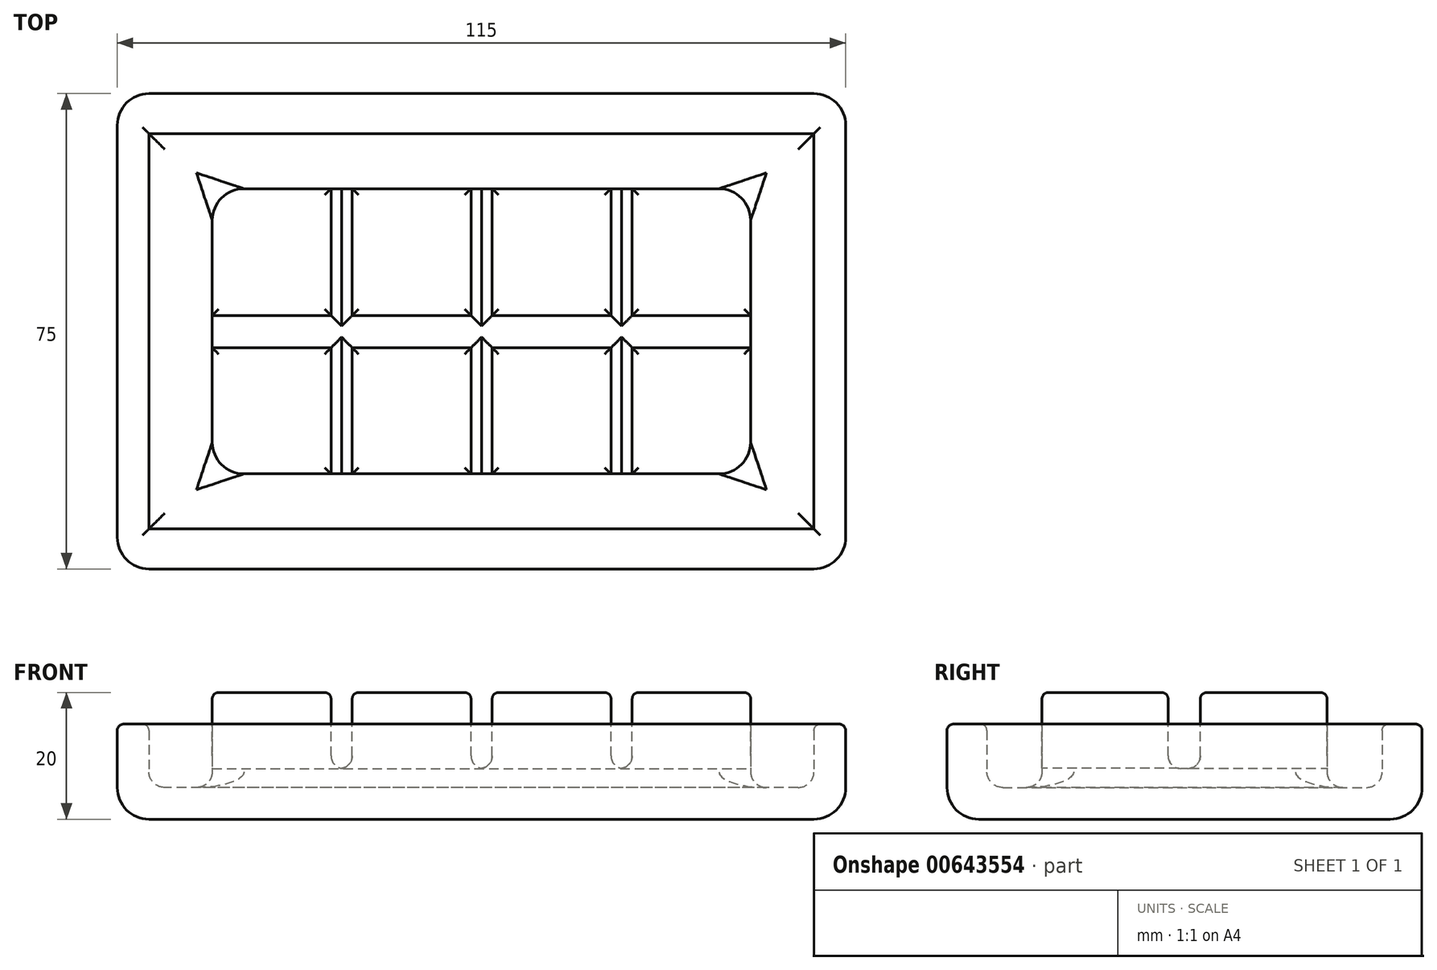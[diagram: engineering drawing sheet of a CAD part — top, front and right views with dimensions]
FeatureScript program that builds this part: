
annotation { "Feature Type Name" : "Feature", "Feature Type Description" : "" }
export const myFeature = defineFeature(function(context is Context, id is Id, definition is map)
    precondition{}
    {
        {
            var Q0;
            Q0=qCreatedBy(makeId("Top.planeOp"),FACE);
            var sketch = newSketch(context, id + "F0", { "sketchPlane" : qUnion([Q0])});
            skLineSegment(sketch, "E0.bottom", {"start": v(57.5, -37.5) * mm, "end": v(-57.5, -37.5) * mm});
            skLineSegment(sketch, "E0.top", {"start": v(57.5, 37.5) * mm, "end": v(-57.5, 37.5) * mm});
            skLineSegment(sketch, "E0.left", {"start": v(57.5, -37.5) * mm, "end": v(57.5, 37.5) * mm});
            skLineSegment(sketch, "E0.right", {"start": v(-57.5, -37.5) * mm, "end": v(-57.5, 37.5) * mm});
            skPoint(sketch, "E0.middle", {"position": v(0, 0) * mm});
            skSolve(sketch);
        }
        {
            var Q0;
            Q0=makeQuery(id+"F0.imprint","IMPRINT",FACE,{"disambiguationData":[TD([[makeQuery(id+"F0.imprint","IMPRINT",EDGE,{"derivedFrom":sQuery(id+"F0.wireOp",EDGE,"E0.bottom")}),-1.0]])]});
            extrude(context, id + "F1", {"entities" : qUnion([Q0]), "depth" : 5 * mm, "offsetDistance" : 25 * mm});
        }
        {
            var Q0;
            Q0=makeQuery(id+"F1.opExtrude","CAP_FACE",FACE,{"disambiguationData":[OSD([sQuery(id+"F0.wireOp",EDGE,"E0.bottom"),sQuery(id+"F0.wireOp",EDGE,"E0.top"),sQuery(id+"F0.wireOp",EDGE,"E0.left"),sQuery(id+"F0.wireOp",EDGE,"E0.right")])],"isStart":false});
            var sketch = newSketch(context, id + "F2", { "sketchPlane" : qUnion([Q0])});
            skLineSegment(sketch, "E1.bottom", {"start": v(52.5, -31.2) * mm, "end": v(-52.5, -31.2) * mm});
            skLineSegment(sketch, "E1.top", {"start": v(52.5, 31.2) * mm, "end": v(-52.5, 31.2) * mm});
            skLineSegment(sketch, "E1.left", {"start": v(52.5, -31.2) * mm, "end": v(52.5, 31.2) * mm});
            skLineSegment(sketch, "E1.right", {"start": v(-52.5, -31.2) * mm, "end": v(-52.5, 31.2) * mm});
            skPoint(sketch, "E1.middle", {"position": v(0, 0) * mm});
            skSolve(sketch);
        }
        {
            var Q0;
            Q0=makeQuery(id+"F2.imprint","IMPRINT",FACE,{"disambiguationData":[TD([[makeQuery(id+"F2.imprint","IMPRINT",EDGE,{"derivedFrom":sQuery(id+"F2.wireOp",EDGE,"E1.bottom")}),1.0]])]});
            extrude(context, id + "F3", {"entities" : qUnion([Q0]), "operationType" : NewBodyOperationType.ADD, "depth" : 10 * mm, "offsetDistance" : 25 * mm});
        }
        {
            var Q0;
            Q0=makeQuery(id+"F1.opExtrude","CAP_FACE",FACE,{"disambiguationData":[OSD([sQuery(id+"F0.wireOp",EDGE,"E0.bottom"),sQuery(id+"F0.wireOp",EDGE,"E0.top"),sQuery(id+"F0.wireOp",EDGE,"E0.left"),sQuery(id+"F0.wireOp",EDGE,"E0.right")])],"isStart":false});
            var sketch = newSketch(context, id + "F4", { "sketchPlane" : qUnion([Q0])});
            skLineSegment(sketch, "E2.bottom", {"start": v(42.5, 22.5) * mm, "end": v(-42.5, 22.5) * mm});
            skLineSegment(sketch, "E2.top", {"start": v(42.5, -22.5) * mm, "end": v(-42.5, -22.5) * mm});
            skLineSegment(sketch, "E2.left", {"start": v(42.5, 22.5) * mm, "end": v(42.5, -22.5) * mm});
            skLineSegment(sketch, "E2.right", {"start": v(-42.5, 22.5) * mm, "end": v(-42.5, -22.5) * mm});
            skPoint(sketch, "E2.middle", {"position": v(0, 0) * mm});
            skSolve(sketch);
        }
        {
            var Q0;
            Q0=makeQuery(id+"F4.imprint","IMPRINT",FACE,{"disambiguationData":[TD([[makeQuery(id+"F4.imprint","IMPRINT",EDGE,{"derivedFrom":sQuery(id+"F4.wireOp",EDGE,"E2.bottom")}),1.0]])]});
            extrude(context, id + "F5", {"entities" : qUnion([Q0]), "operationType" : NewBodyOperationType.ADD, "depth" : 15 * mm, "offsetDistance" : 25 * mm});
        }
        {
            var Q0;
            Q0=makeQuery(id+"F5.opExtrude","CAP_FACE",FACE,{"disambiguationData":[OSD([sQuery(id+"F4.wireOp",EDGE,"E2.bottom"),sQuery(id+"F4.wireOp",EDGE,"E2.top"),sQuery(id+"F4.wireOp",EDGE,"E2.left"),sQuery(id+"F4.wireOp",EDGE,"E2.right")])],"isStart":false});
            var sketch = newSketch(context, id + "F6", { "sketchPlane" : qUnion([Q0])});
            skLineSegment(sketch, "E3.bottom", {"start": v(-42.5, 22.5) * mm, "end": v(-23.75, 22.5) * mm});
            skLineSegment(sketch, "E3.top", {"start": v(-42.5, 2.5) * mm, "end": v(-23.75, 2.5) * mm});
            skLineSegment(sketch, "E3.left", {"start": v(-42.5, 22.5) * mm, "end": v(-42.5, 2.5) * mm});
            skLineSegment(sketch, "E3.right", {"start": v(-23.75, 22.5) * mm, "end": v(-23.75, 2.5) * mm});
            skLineSegment(sketch, "E4.0.1.0", {"start": v(-42.5, -2.6) * mm, "end": v(-23.75, -2.6) * mm});
            skLineSegment(sketch, "E4.0.1.1", {"start": v(-23.75, -2.6) * mm, "end": v(-23.75, -22.6) * mm});
            skLineSegment(sketch, "E4.0.1.2", {"start": v(-42.5, -22.6) * mm, "end": v(-23.75, -22.6) * mm});
            skLineSegment(sketch, "E4.0.1.3", {"start": v(-42.5, -2.6) * mm, "end": v(-42.5, -22.6) * mm});
            skLineSegment(sketch, "E4.1.0.0", {"start": v(-20.4, 22.5) * mm, "end": v(-1.65, 22.5) * mm});
            skLineSegment(sketch, "E4.1.0.1", {"start": v(-1.65, 22.5) * mm, "end": v(-1.65, 2.5) * mm});
            skLineSegment(sketch, "E4.1.0.2", {"start": v(-20.4, 2.5) * mm, "end": v(-1.65, 2.5) * mm});
            skLineSegment(sketch, "E4.1.0.3", {"start": v(-20.4, 22.5) * mm, "end": v(-20.4, 2.5) * mm});
            skLineSegment(sketch, "E4.1.1.0", {"start": v(-20.4, -2.6) * mm, "end": v(-1.65, -2.6) * mm});
            skLineSegment(sketch, "E4.1.1.1", {"start": v(-1.65, -2.6) * mm, "end": v(-1.65, -22.6) * mm});
            skLineSegment(sketch, "E4.1.1.2", {"start": v(-20.4, -22.6) * mm, "end": v(-1.65, -22.6) * mm});
            skLineSegment(sketch, "E4.1.1.3", {"start": v(-20.4, -2.6) * mm, "end": v(-20.4, -22.6) * mm});
            skLineSegment(sketch, "E4.2.0.0", {"start": v(1.7, 22.5) * mm, "end": v(20.45, 22.5) * mm});
            skLineSegment(sketch, "E4.2.0.1", {"start": v(20.45, 22.5) * mm, "end": v(20.45, 2.5) * mm});
            skLineSegment(sketch, "E4.2.0.2", {"start": v(1.7, 2.5) * mm, "end": v(20.45, 2.5) * mm});
            skLineSegment(sketch, "E4.2.0.3", {"start": v(1.7, 22.5) * mm, "end": v(1.7, 2.5) * mm});
            skLineSegment(sketch, "E4.2.1.0", {"start": v(1.7, -2.6) * mm, "end": v(20.45, -2.6) * mm});
            skLineSegment(sketch, "E4.2.1.1", {"start": v(20.45, -2.6) * mm, "end": v(20.45, -22.6) * mm});
            skLineSegment(sketch, "E4.2.1.2", {"start": v(1.7, -22.6) * mm, "end": v(20.45, -22.6) * mm});
            skLineSegment(sketch, "E4.2.1.3", {"start": v(1.7, -2.6) * mm, "end": v(1.7, -22.6) * mm});
            skLineSegment(sketch, "E4.3.0.0", {"start": v(23.8, 22.5) * mm, "end": v(42.55, 22.5) * mm});
            skLineSegment(sketch, "E4.3.0.1", {"start": v(42.55, 22.5) * mm, "end": v(42.55, 2.5) * mm});
            skLineSegment(sketch, "E4.3.0.2", {"start": v(23.8, 2.5) * mm, "end": v(42.55, 2.5) * mm});
            skLineSegment(sketch, "E4.3.0.3", {"start": v(23.8, 22.5) * mm, "end": v(23.8, 2.5) * mm});
            skLineSegment(sketch, "E4.3.1.0", {"start": v(23.8, -2.6) * mm, "end": v(42.55, -2.6) * mm});
            skLineSegment(sketch, "E4.3.1.1", {"start": v(42.55, -2.6) * mm, "end": v(42.55, -22.6) * mm});
            skLineSegment(sketch, "E4.3.1.2", {"start": v(23.8, -22.6) * mm, "end": v(42.55, -22.6) * mm});
            skLineSegment(sketch, "E4.3.1.3", {"start": v(23.8, -2.6) * mm, "end": v(23.8, -22.6) * mm});
            skLineSegment(sketch, "E4.direction1", {"start": v(-42.5, 22.5) * mm, "end": v(-20.4, 22.5) * mm, "construction": true});
            skLineSegment(sketch, "E4.direction2", {"start": v(-42.5, 22.5) * mm, "end": v(-42.5, -2.6) * mm, "construction": true});
            skSolve(sketch);
        }
        {
            var Q0;
            {var subQ20=sQuery(id+"F6.wireOp",EDGE,"E3.top");Q0=makeQuery(id+"F6.imprint","IMPRINT",FACE,{"disambiguationData":[TD([[makeQuery(id+"F6.imprint","IMPRINT",EDGE,{"derivedFrom":subQ20}),-1.0]])]});}
            var Q1;
            Q1 = qConstructionFilter(qBodyType(qCreatedBy(id + "F6" ,EDGE), BodyType.WIRE), ConstructionObject.NO);
            extrude(context, id + "F7", {"entities" : qUnion([Q0]), "operationType" : NewBodyOperationType.REMOVE, "surfaceEntities" : qUnion([Q1]), "oppositeDirection" : true, "depth" : 12 * mm, "offsetDistance" : 25 * mm});
        }
        {
            var Q0;
            Q0=makeQuery(id+"F1.opExtrude","CAP_FACE",FACE,{"disambiguationData":[OSD([sQuery(id+"F0.wireOp",EDGE,"E0.bottom"),sQuery(id+"F0.wireOp",EDGE,"E0.top"),sQuery(id+"F0.wireOp",EDGE,"E0.left"),sQuery(id+"F0.wireOp",EDGE,"E0.right")])],"isStart":false});
            fillet(context, id + "F8", {"entities" : qUnion([Q0]), "radius" : 2.5 * mm, "tangentPropagation" : true, "allowEdgeOverflow" : false});
        }
        {
            var Q0;
            Q0=makeQuery(id+"F5.opExtrude","SWEPT_EDGE",EDGE,{"disambiguationData":[OSD([sQuery(id+"F4.wireOp",EDGE,"E2.bottom"),sQuery(id+"F4.wireOp",EDGE,"E2.right")])]});
            var Q1;
            Q1=makeQuery(id+"F5.opExtrude","SWEPT_EDGE",EDGE,{"disambiguationData":[OSD([sQuery(id+"F4.wireOp",EDGE,"E2.bottom"),sQuery(id+"F4.wireOp",EDGE,"E2.left")])]});
            var Q2;
            Q2=makeQuery(id+"F5.opExtrude","SWEPT_EDGE",EDGE,{"disambiguationData":[OSD([sQuery(id+"F4.wireOp",EDGE,"E2.top"),sQuery(id+"F4.wireOp",EDGE,"E2.right")])]});
            var Q3;
            Q3=makeQuery(id+"F5.opExtrude","SWEPT_EDGE",EDGE,{"disambiguationData":[OSD([sQuery(id+"F4.wireOp",EDGE,"E2.top"),sQuery(id+"F4.wireOp",EDGE,"E2.left")])]});
            fillet(context, id + "F9", {"entities" : qUnion([Q0, Q1, Q2, Q3]), "radius" : 5 * mm, "tangentPropagation" : true, "allowEdgeOverflow" : false});
        }
        {
            var Q0;
            Q0=makeQuery(id+"F3.opExtrude","CAP_FACE",FACE,{"disambiguationData":[OSD([sQuery(id+"F0.wireOp",EDGE,"E0.bottom"),sQuery(id+"F0.wireOp",EDGE,"E0.top"),sQuery(id+"F0.wireOp",EDGE,"E0.left"),sQuery(id+"F0.wireOp",EDGE,"E0.right"),sQuery(id+"F2.wireOp",EDGE,"E1.bottom"),sQuery(id+"F2.wireOp",EDGE,"E1.top"),sQuery(id+"F2.wireOp",EDGE,"E1.left"),sQuery(id+"F2.wireOp",EDGE,"E1.right")])],"isStart":false});
            var Q1;
            {var subQ0=sQuery(id+"F4.wireOp",EDGE,"E2.bottom");var subQ1=sQuery(id+"F4.wireOp",EDGE,"E2.right");Q1=makeQuery(id+"FAPkeNOE4h7F2cH_1.boolean.opBoolean","SPLIT",FACE,{"disambiguationData":[TD([makeQuery(id+"FAPkeNOE4h7F2cH_1.opExtrude","SWEPT_FACE",FACE,{"disambiguationData":[OSD([sQuery(id+"FX66zExsaY10lFn_1.wireOp",EDGE,"empMxAXI-gNUu-jkWw-ZaRX-JOoaTAKe9f3l.top")])]})])],"derivedFrom":makeQuery(id+"F5.opExtrude","CAP_FACE",FACE,{"disambiguationData":[OSD([subQ0,sQuery(id+"F4.wireOp",EDGE,"E2.top"),sQuery(id+"F4.wireOp",EDGE,"E2.left"),subQ1])],"isStart":false})});}
            var Q2;
            {var subQ0=sQuery(id+"F4.wireOp",EDGE,"E2.bottom");Q2=makeQuery(id+"FAPkeNOE4h7F2cH_1.boolean.opBoolean","SPLIT",FACE,{"disambiguationData":[TD([makeQuery(id+"FAPkeNOE4h7F2cH_1.opExtrude","SWEPT_FACE",FACE,{"disambiguationData":[OSD([sQuery(id+"FX66zExsaY10lFn_1.wireOp",EDGE,"7448a35d-e1ee-42d6-8efa-172e43eae52a.1.0.1")])]})])],"derivedFrom":makeQuery(id+"F5.opExtrude","CAP_FACE",FACE,{"disambiguationData":[OSD([subQ0,sQuery(id+"F4.wireOp",EDGE,"E2.top"),sQuery(id+"F4.wireOp",EDGE,"E2.left"),sQuery(id+"F4.wireOp",EDGE,"E2.right")])],"isStart":false})});}
            var Q3;
            {var subQ0=sQuery(id+"F4.wireOp",EDGE,"E2.bottom");Q3=makeQuery(id+"FAPkeNOE4h7F2cH_1.boolean.opBoolean","SPLIT",FACE,{"disambiguationData":[TD([makeQuery(id+"FAPkeNOE4h7F2cH_1.opExtrude","SWEPT_FACE",FACE,{"disambiguationData":[OSD([sQuery(id+"FX66zExsaY10lFn_1.wireOp",EDGE,"7448a35d-e1ee-42d6-8efa-172e43eae52a.2.0.1")])]})])],"derivedFrom":makeQuery(id+"F5.opExtrude","CAP_FACE",FACE,{"disambiguationData":[OSD([subQ0,sQuery(id+"F4.wireOp",EDGE,"E2.top"),sQuery(id+"F4.wireOp",EDGE,"E2.left"),sQuery(id+"F4.wireOp",EDGE,"E2.right")])],"isStart":false})});}
            var Q4;
            {var subQ0=sQuery(id+"F4.wireOp",EDGE,"E2.bottom");var subQ1=sQuery(id+"F4.wireOp",EDGE,"E2.left");Q4=makeQuery(id+"FAPkeNOE4h7F2cH_1.boolean.opBoolean","SPLIT",FACE,{"disambiguationData":[TD([makeQuery(id+"FAPkeNOE4h7F2cH_1.opExtrude","SWEPT_FACE",FACE,{"disambiguationData":[OSD([sQuery(id+"FX66zExsaY10lFn_1.wireOp",EDGE,"7448a35d-e1ee-42d6-8efa-172e43eae52a.3.0.2")])]})])],"derivedFrom":makeQuery(id+"F5.opExtrude","CAP_FACE",FACE,{"disambiguationData":[OSD([subQ0,sQuery(id+"F4.wireOp",EDGE,"E2.top"),subQ1,sQuery(id+"F4.wireOp",EDGE,"E2.right")])],"isStart":false})});}
            var Q5;
            {var subQ0=sQuery(id+"F4.wireOp",EDGE,"E2.left");Q5=makeQuery(id+"FAPkeNOE4h7F2cH_1.boolean.opBoolean","SPLIT",FACE,{"disambiguationData":[TD([makeQuery(id+"FAPkeNOE4h7F2cH_1.opExtrude","SWEPT_FACE",FACE,{"disambiguationData":[OSD([sQuery(id+"FX66zExsaY10lFn_1.wireOp",EDGE,"7448a35d-e1ee-42d6-8efa-172e43eae52a.3.1.0")])]})])],"derivedFrom":makeQuery(id+"F5.opExtrude","CAP_FACE",FACE,{"disambiguationData":[OSD([sQuery(id+"F4.wireOp",EDGE,"E2.bottom"),sQuery(id+"F4.wireOp",EDGE,"E2.top"),subQ0,sQuery(id+"F4.wireOp",EDGE,"E2.right")])],"isStart":false})});}
            var Q6;
            {var subQ0=sQuery(id+"F4.wireOp",EDGE,"E2.left");Q6=makeQuery(id+"FAPkeNOE4h7F2cH_1.boolean.opBoolean","SPLIT",FACE,{"disambiguationData":[TD([makeQuery(id+"FAPkeNOE4h7F2cH_1.opExtrude","SWEPT_FACE",FACE,{"disambiguationData":[OSD([sQuery(id+"FX66zExsaY10lFn_1.wireOp",EDGE,"7448a35d-e1ee-42d6-8efa-172e43eae52a.3.2.0")])]})])],"derivedFrom":makeQuery(id+"F5.opExtrude","CAP_FACE",FACE,{"disambiguationData":[OSD([sQuery(id+"F4.wireOp",EDGE,"E2.bottom"),sQuery(id+"F4.wireOp",EDGE,"E2.top"),subQ0,sQuery(id+"F4.wireOp",EDGE,"E2.right")])],"isStart":false})});}
            var Q7;
            Q7=makeQuery(id+"FAPkeNOE4h7F2cH_1.boolean.opBoolean","SPLIT",FACE,{"disambiguationData":[TD([makeQuery(id+"FAPkeNOE4h7F2cH_1.opExtrude","SWEPT_FACE",FACE,{"disambiguationData":[OSD([sQuery(id+"FX66zExsaY10lFn_1.wireOp",EDGE,"7448a35d-e1ee-42d6-8efa-172e43eae52a.2.2.0")])]})])],"derivedFrom":makeQuery(id+"F5.opExtrude","CAP_FACE",FACE,{"disambiguationData":[OSD([sQuery(id+"F4.wireOp",EDGE,"E2.bottom"),sQuery(id+"F4.wireOp",EDGE,"E2.top"),sQuery(id+"F4.wireOp",EDGE,"E2.left"),sQuery(id+"F4.wireOp",EDGE,"E2.right")])],"isStart":false})});
            var Q8;
            Q8=makeQuery(id+"FAPkeNOE4h7F2cH_1.boolean.opBoolean","SPLIT",FACE,{"disambiguationData":[TD([makeQuery(id+"FAPkeNOE4h7F2cH_1.opExtrude","SWEPT_FACE",FACE,{"disambiguationData":[OSD([sQuery(id+"FX66zExsaY10lFn_1.wireOp",EDGE,"7448a35d-e1ee-42d6-8efa-172e43eae52a.2.1.0")])]})])],"derivedFrom":makeQuery(id+"F5.opExtrude","CAP_FACE",FACE,{"disambiguationData":[OSD([sQuery(id+"F4.wireOp",EDGE,"E2.bottom"),sQuery(id+"F4.wireOp",EDGE,"E2.top"),sQuery(id+"F4.wireOp",EDGE,"E2.left"),sQuery(id+"F4.wireOp",EDGE,"E2.right")])],"isStart":false})});
            var Q9;
            Q9=makeQuery(id+"FAPkeNOE4h7F2cH_1.boolean.opBoolean","SPLIT",FACE,{"disambiguationData":[TD([makeQuery(id+"FAPkeNOE4h7F2cH_1.opExtrude","SWEPT_FACE",FACE,{"disambiguationData":[OSD([sQuery(id+"FX66zExsaY10lFn_1.wireOp",EDGE,"7448a35d-e1ee-42d6-8efa-172e43eae52a.1.1.0")])]})])],"derivedFrom":makeQuery(id+"F5.opExtrude","CAP_FACE",FACE,{"disambiguationData":[OSD([sQuery(id+"F4.wireOp",EDGE,"E2.bottom"),sQuery(id+"F4.wireOp",EDGE,"E2.top"),sQuery(id+"F4.wireOp",EDGE,"E2.left"),sQuery(id+"F4.wireOp",EDGE,"E2.right")])],"isStart":false})});
            var Q10;
            Q10=makeQuery(id+"FAPkeNOE4h7F2cH_1.boolean.opBoolean","SPLIT",FACE,{"disambiguationData":[TD([makeQuery(id+"FAPkeNOE4h7F2cH_1.opExtrude","SWEPT_FACE",FACE,{"disambiguationData":[OSD([sQuery(id+"FX66zExsaY10lFn_1.wireOp",EDGE,"7448a35d-e1ee-42d6-8efa-172e43eae52a.1.2.0")])]})])],"derivedFrom":makeQuery(id+"F5.opExtrude","CAP_FACE",FACE,{"disambiguationData":[OSD([sQuery(id+"F4.wireOp",EDGE,"E2.bottom"),sQuery(id+"F4.wireOp",EDGE,"E2.top"),sQuery(id+"F4.wireOp",EDGE,"E2.left"),sQuery(id+"F4.wireOp",EDGE,"E2.right")])],"isStart":false})});
            var Q11;
            {var subQ0=sQuery(id+"F4.wireOp",EDGE,"E2.right");Q11=makeQuery(id+"FAPkeNOE4h7F2cH_1.boolean.opBoolean","SPLIT",FACE,{"disambiguationData":[TD([makeQuery(id+"FAPkeNOE4h7F2cH_1.opExtrude","SWEPT_FACE",FACE,{"disambiguationData":[OSD([sQuery(id+"FX66zExsaY10lFn_1.wireOp",EDGE,"7448a35d-e1ee-42d6-8efa-172e43eae52a.0.1.0")])]})])],"derivedFrom":makeQuery(id+"F5.opExtrude","CAP_FACE",FACE,{"disambiguationData":[OSD([sQuery(id+"F4.wireOp",EDGE,"E2.bottom"),sQuery(id+"F4.wireOp",EDGE,"E2.top"),sQuery(id+"F4.wireOp",EDGE,"E2.left"),subQ0])],"isStart":false})});}
            var Q12;
            {var subQ0=sQuery(id+"F4.wireOp",EDGE,"E2.right");Q12=makeQuery(id+"FAPkeNOE4h7F2cH_1.boolean.opBoolean","SPLIT",FACE,{"disambiguationData":[TD([makeQuery(id+"FAPkeNOE4h7F2cH_1.opExtrude","SWEPT_FACE",FACE,{"disambiguationData":[OSD([sQuery(id+"FX66zExsaY10lFn_1.wireOp",EDGE,"7448a35d-e1ee-42d6-8efa-172e43eae52a.0.2.0")])]})])],"derivedFrom":makeQuery(id+"F5.opExtrude","CAP_FACE",FACE,{"disambiguationData":[OSD([sQuery(id+"F4.wireOp",EDGE,"E2.bottom"),sQuery(id+"F4.wireOp",EDGE,"E2.top"),sQuery(id+"F4.wireOp",EDGE,"E2.left"),subQ0])],"isStart":false})});}
            var Q13;
            {var subQ0=sQuery(id+"F4.wireOp",EDGE,"E2.top");var subQ1=sQuery(id+"F4.wireOp",EDGE,"E2.right");Q13=makeQuery(id+"FAPkeNOE4h7F2cH_1.boolean.opBoolean","SPLIT",FACE,{"disambiguationData":[TD([makeQuery(id+"FAPkeNOE4h7F2cH_1.opExtrude","SWEPT_FACE",FACE,{"disambiguationData":[OSD([sQuery(id+"FX66zExsaY10lFn_1.wireOp",EDGE,"7448a35d-e1ee-42d6-8efa-172e43eae52a.0.3.0")])]})])],"derivedFrom":makeQuery(id+"F5.opExtrude","CAP_FACE",FACE,{"disambiguationData":[OSD([sQuery(id+"F4.wireOp",EDGE,"E2.bottom"),subQ0,sQuery(id+"F4.wireOp",EDGE,"E2.left"),subQ1])],"isStart":false})});}
            var Q14;
            {var subQ0=sQuery(id+"F4.wireOp",EDGE,"E2.top");Q14=makeQuery(id+"FAPkeNOE4h7F2cH_1.boolean.opBoolean","SPLIT",FACE,{"disambiguationData":[TD([makeQuery(id+"FAPkeNOE4h7F2cH_1.opExtrude","SWEPT_FACE",FACE,{"disambiguationData":[OSD([sQuery(id+"FX66zExsaY10lFn_1.wireOp",EDGE,"7448a35d-e1ee-42d6-8efa-172e43eae52a.1.3.0")])]})])],"derivedFrom":makeQuery(id+"F5.opExtrude","CAP_FACE",FACE,{"disambiguationData":[OSD([sQuery(id+"F4.wireOp",EDGE,"E2.bottom"),subQ0,sQuery(id+"F4.wireOp",EDGE,"E2.left"),sQuery(id+"F4.wireOp",EDGE,"E2.right")])],"isStart":false})});}
            var Q15;
            {var subQ0=sQuery(id+"F4.wireOp",EDGE,"E2.top");Q15=makeQuery(id+"FAPkeNOE4h7F2cH_1.boolean.opBoolean","SPLIT",FACE,{"disambiguationData":[TD([makeQuery(id+"FAPkeNOE4h7F2cH_1.opExtrude","SWEPT_FACE",FACE,{"disambiguationData":[OSD([sQuery(id+"FX66zExsaY10lFn_1.wireOp",EDGE,"7448a35d-e1ee-42d6-8efa-172e43eae52a.2.3.0")])]})])],"derivedFrom":makeQuery(id+"F5.opExtrude","CAP_FACE",FACE,{"disambiguationData":[OSD([sQuery(id+"F4.wireOp",EDGE,"E2.bottom"),subQ0,sQuery(id+"F4.wireOp",EDGE,"E2.left"),sQuery(id+"F4.wireOp",EDGE,"E2.right")])],"isStart":false})});}
            var Q16;
            {var subQ0=sQuery(id+"F4.wireOp",EDGE,"E2.top");var subQ1=sQuery(id+"F4.wireOp",EDGE,"E2.left");Q16=makeQuery(id+"FAPkeNOE4h7F2cH_1.boolean.opBoolean","SPLIT",FACE,{"disambiguationData":[TD([makeQuery(id+"FAPkeNOE4h7F2cH_1.opExtrude","SWEPT_FACE",FACE,{"disambiguationData":[OSD([sQuery(id+"FX66zExsaY10lFn_1.wireOp",EDGE,"7448a35d-e1ee-42d6-8efa-172e43eae52a.3.3.0")])]})])],"derivedFrom":makeQuery(id+"F5.opExtrude","CAP_FACE",FACE,{"disambiguationData":[OSD([sQuery(id+"F4.wireOp",EDGE,"E2.bottom"),subQ0,subQ1,sQuery(id+"F4.wireOp",EDGE,"E2.right")])],"isStart":false})});}
            fillet(context, id + "F10", {"entities" : qUnion([Q0, Q1, Q2, Q3, Q4, Q5, Q6, Q7, Q8, Q9, Q10, Q11, Q12, Q13, Q14, Q15, Q16]), "radius" : 1 * mm, "tangentPropagation" : true, "allowEdgeOverflow" : false});
        }
        {
            var Q0;
            {var subQ0=sQuery(id+"F0.wireOp",EDGE,"E0.left");var subQ1=sQuery(id+"F0.wireOp",EDGE,"E0.bottom");Q0=makeQuery(id+"F3.boolean.opBoolean","MERGE",EDGE,{"derivedFrom":[makeQuery(id+"F1.opExtrude","SWEPT_EDGE",EDGE,{"disambiguationData":[OSD([subQ1,subQ0])]}),makeQuery(id+"F3.opExtrude","SWEPT_EDGE",EDGE,{"disambiguationData":[OSD([subQ1,subQ0])]})]});}
            var Q1;
            {var subQ0=sQuery(id+"F0.wireOp",EDGE,"E0.left");var subQ1=sQuery(id+"F0.wireOp",EDGE,"E0.top");Q1=makeQuery(id+"F3.boolean.opBoolean","MERGE",EDGE,{"derivedFrom":[makeQuery(id+"F1.opExtrude","SWEPT_EDGE",EDGE,{"disambiguationData":[OSD([subQ1,subQ0])]}),makeQuery(id+"F3.opExtrude","SWEPT_EDGE",EDGE,{"disambiguationData":[OSD([subQ1,subQ0])]})]});}
            var Q2;
            {var subQ0=sQuery(id+"F0.wireOp",EDGE,"E0.right");var subQ1=sQuery(id+"F0.wireOp",EDGE,"E0.top");Q2=makeQuery(id+"F3.boolean.opBoolean","MERGE",EDGE,{"derivedFrom":[makeQuery(id+"F1.opExtrude","SWEPT_EDGE",EDGE,{"disambiguationData":[OSD([subQ1,subQ0])]}),makeQuery(id+"F3.opExtrude","SWEPT_EDGE",EDGE,{"disambiguationData":[OSD([subQ1,subQ0])]})]});}
            var Q3;
            Q3=makeQuery(id+"F1.opExtrude","CAP_EDGE",EDGE,{"disambiguationData":[OSD([sQuery(id+"F0.wireOp",EDGE,"E0.top")])],"isStart":true});
            var Q4;
            Q4=makeQuery(id+"F1.opExtrude","CAP_EDGE",EDGE,{"disambiguationData":[OSD([sQuery(id+"F0.wireOp",EDGE,"E0.left")])],"isStart":true});
            var Q5;
            Q5=makeQuery(id+"F1.opExtrude","CAP_EDGE",EDGE,{"disambiguationData":[OSD([sQuery(id+"F0.wireOp",EDGE,"E0.bottom")])],"isStart":true});
            var Q6;
            Q6=makeQuery(id+"F1.opExtrude","CAP_EDGE",EDGE,{"disambiguationData":[OSD([sQuery(id+"F0.wireOp",EDGE,"E0.right")])],"isStart":true});
            var Q7;
            {var subQ0=sQuery(id+"F0.wireOp",EDGE,"E0.right");var subQ1=sQuery(id+"F0.wireOp",EDGE,"E0.bottom");Q7=makeQuery(id+"F3.boolean.opBoolean","MERGE",EDGE,{"derivedFrom":[makeQuery(id+"F1.opExtrude","SWEPT_EDGE",EDGE,{"disambiguationData":[OSD([subQ1,subQ0])]}),makeQuery(id+"F3.opExtrude","SWEPT_EDGE",EDGE,{"disambiguationData":[OSD([subQ1,subQ0])]})]});}
            fillet(context, id + "F11", {"entities" : qUnion([Q0, Q1, Q2, Q3, Q4, Q5, Q6, Q7]), "radius" : 5 * mm, "tangentPropagation" : true, "allowEdgeOverflow" : false});
        }
        {
            var Q0;
            Q0=makeQuery(id+"F7.boolean.opBoolean","COPY",EDGE,{"derivedFrom":makeQuery(id+"F7.opExtrude","CAP_EDGE",EDGE,{"disambiguationData":[OSD([sQuery(id+"F6.wireOp",EDGE,"E3.right")])],"isStart":false})});
            var Q1;
            Q1=makeQuery(id+"F7.boolean.opBoolean","COPY",EDGE,{"derivedFrom":makeQuery(id+"F7.opExtrude","CAP_EDGE",EDGE,{"disambiguationData":[OSD([sQuery(id+"F6.wireOp",EDGE,"E3.top")])],"isStart":false})});
            var Q2;
            Q2=makeQuery(id+"F7.boolean.opBoolean","COPY",EDGE,{"derivedFrom":makeQuery(id+"F7.opExtrude","CAP_EDGE",EDGE,{"disambiguationData":[OSD([sQuery(id+"F6.wireOp",EDGE,"E4.1.0.2")])],"isStart":false})});
            var Q3;
            Q3=makeQuery(id+"F7.boolean.opBoolean","COPY",EDGE,{"derivedFrom":makeQuery(id+"F7.opExtrude","CAP_EDGE",EDGE,{"disambiguationData":[OSD([sQuery(id+"F6.wireOp",EDGE,"E4.1.0.1")])],"isStart":false})});
            var Q4;
            Q4=makeQuery(id+"F7.boolean.opBoolean","COPY",EDGE,{"derivedFrom":makeQuery(id+"F7.opExtrude","CAP_EDGE",EDGE,{"disambiguationData":[OSD([sQuery(id+"F6.wireOp",EDGE,"E4.2.0.2")])],"isStart":false})});
            var Q5;
            Q5=makeQuery(id+"F7.boolean.opBoolean","COPY",EDGE,{"derivedFrom":makeQuery(id+"F7.opExtrude","CAP_EDGE",EDGE,{"disambiguationData":[OSD([sQuery(id+"F6.wireOp",EDGE,"E4.2.0.1")])],"isStart":false})});
            var Q6;
            Q6=makeQuery(id+"F7.boolean.opBoolean","COPY",EDGE,{"derivedFrom":makeQuery(id+"F7.opExtrude","CAP_EDGE",EDGE,{"disambiguationData":[OSD([sQuery(id+"F6.wireOp",EDGE,"E4.3.0.2")])],"isStart":false})});
            var Q7;
            Q7=makeQuery(id+"F7.boolean.opBoolean","COPY",EDGE,{"derivedFrom":makeQuery(id+"F7.opExtrude","CAP_EDGE",EDGE,{"disambiguationData":[OSD([sQuery(id+"F6.wireOp",EDGE,"E4.2.1.1")])],"isStart":false})});
            var Q8;
            Q8=makeQuery(id+"F7.boolean.opBoolean","COPY",EDGE,{"derivedFrom":makeQuery(id+"F7.opExtrude","CAP_EDGE",EDGE,{"disambiguationData":[OSD([sQuery(id+"F6.wireOp",EDGE,"E4.1.0.3")])],"isStart":false})});
            var Q9;
            Q9=makeQuery(id+"F7.boolean.opBoolean","COPY",EDGE,{"derivedFrom":makeQuery(id+"F7.opExtrude","CAP_EDGE",EDGE,{"disambiguationData":[OSD([sQuery(id+"F6.wireOp",EDGE,"E4.2.0.3")])],"isStart":false})});
            var Q10;
            Q10=makeQuery(id+"F7.boolean.opBoolean","COPY",EDGE,{"derivedFrom":makeQuery(id+"F7.opExtrude","CAP_EDGE",EDGE,{"disambiguationData":[OSD([sQuery(id+"F6.wireOp",EDGE,"E4.3.0.3")])],"isStart":false})});
            var Q11;
            Q11=makeQuery(id+"F7.boolean.opBoolean","COPY",EDGE,{"derivedFrom":makeQuery(id+"F7.opExtrude","CAP_EDGE",EDGE,{"disambiguationData":[OSD([sQuery(id+"F6.wireOp",EDGE,"E4.3.1.0")])],"isStart":false})});
            var Q12;
            Q12=makeQuery(id+"F7.boolean.opBoolean","COPY",EDGE,{"derivedFrom":makeQuery(id+"F7.opExtrude","CAP_EDGE",EDGE,{"disambiguationData":[OSD([sQuery(id+"F6.wireOp",EDGE,"E4.3.1.3")])],"isStart":false})});
            var Q13;
            Q13=makeQuery(id+"F7.boolean.opBoolean","COPY",EDGE,{"derivedFrom":makeQuery(id+"F7.opExtrude","CAP_EDGE",EDGE,{"disambiguationData":[OSD([sQuery(id+"F6.wireOp",EDGE,"E4.2.1.0")])],"isStart":false})});
            var Q14;
            Q14=makeQuery(id+"F7.boolean.opBoolean","COPY",EDGE,{"derivedFrom":makeQuery(id+"F7.opExtrude","CAP_EDGE",EDGE,{"disambiguationData":[OSD([sQuery(id+"F6.wireOp",EDGE,"E4.2.1.3")])],"isStart":false})});
            var Q15;
            Q15=makeQuery(id+"F7.boolean.opBoolean","COPY",EDGE,{"derivedFrom":makeQuery(id+"F7.opExtrude","CAP_EDGE",EDGE,{"disambiguationData":[OSD([sQuery(id+"F6.wireOp",EDGE,"E4.1.1.0")])],"isStart":false})});
            var Q16;
            Q16=makeQuery(id+"F7.boolean.opBoolean","COPY",EDGE,{"derivedFrom":makeQuery(id+"F7.opExtrude","CAP_EDGE",EDGE,{"disambiguationData":[OSD([sQuery(id+"F6.wireOp",EDGE,"E4.1.1.3")])],"isStart":false})});
            var Q17;
            Q17=makeQuery(id+"F7.boolean.opBoolean","COPY",EDGE,{"derivedFrom":makeQuery(id+"F7.opExtrude","CAP_EDGE",EDGE,{"disambiguationData":[OSD([sQuery(id+"F6.wireOp",EDGE,"E4.0.1.0")])],"isStart":false})});
            var Q18;
            Q18=makeQuery(id+"F7.boolean.opBoolean","COPY",EDGE,{"derivedFrom":makeQuery(id+"F7.opExtrude","CAP_EDGE",EDGE,{"disambiguationData":[OSD([sQuery(id+"F6.wireOp",EDGE,"E4.1.1.1")])],"isStart":false})});
            var Q19;
            Q19=makeQuery(id+"F7.boolean.opBoolean","COPY",EDGE,{"derivedFrom":makeQuery(id+"F7.opExtrude","CAP_EDGE",EDGE,{"disambiguationData":[OSD([sQuery(id+"F6.wireOp",EDGE,"E4.0.1.1")])],"isStart":false})});
            fillet(context, id + "F12", {"entities" : qUnion([Q0, Q1, Q2, Q3, Q4, Q5, Q6, Q7, Q8, Q9, Q10, Q11, Q12, Q13, Q14, Q15, Q16, Q17, Q18, Q19]), "radius" : 2 * mm, "tangentPropagation" : true, "allowEdgeOverflow" : false});
        }
    });
